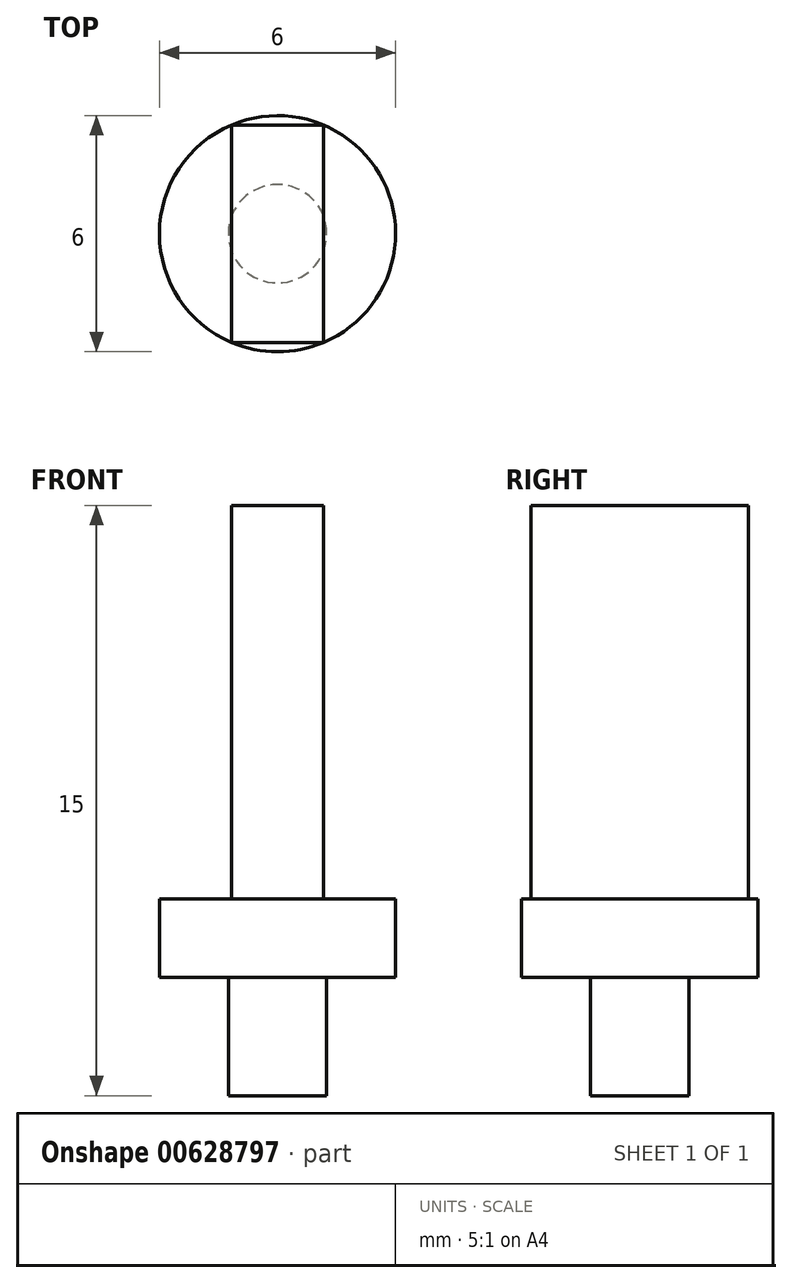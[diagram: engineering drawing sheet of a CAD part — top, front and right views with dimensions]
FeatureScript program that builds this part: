
annotation { "Feature Type Name" : "Feature", "Feature Type Description" : "" }
export const myFeature = defineFeature(function(context is Context, id is Id, definition is map)
    precondition{}
    {
        {
            var Q0;
            Q0=qCreatedBy(makeId("Top.planeOp"),FACE);
            var sketch = newSketch(context, id + "F0", { "sketchPlane" : qUnion([Q0])});
            skCircle(sketch, "E0", {"center": v(0, 0) * mm, "radius": 1.25 * mm});
            skSolve(sketch);
        }
        {
            var Q0;
            Q0 = qSketchRegion(id + "F0", true);
            extrude(context, id + "F1", {"entities" : qUnion([Q0]), "depth" : 3 * mm, "offsetDistance" : 25 * mm});
        }
        {
            var Q0;
            Q0=makeQuery(id+"F1.opExtrude","CAP_FACE",FACE,{"disambiguationData":[OSD([sQuery(id+"F0.wireOp",EDGE,"E0")])],"isStart":false});
            var sketch = newSketch(context, id + "F2", { "sketchPlane" : qUnion([Q0])});
            skCircle(sketch, "E1", {"center": v(0, 0) * mm, "radius": 3 * mm});
            skSolve(sketch);
        }
        {
            var Q0;
            Q0 = qSketchRegion(id + "F2", true);
            extrude(context, id + "F3", {"entities" : qUnion([Q0]), "operationType" : NewBodyOperationType.ADD, "depth" : 2 * mm, "offsetDistance" : 25 * mm});
        }
        {
            var Q0;
            Q0=makeQuery(id+"F3.opExtrude","CAP_FACE",FACE,{"disambiguationData":[OSD([sQuery(id+"F2.wireOp",EDGE,"E1")])],"isStart":false});
            var sketch = newSketch(context, id + "F4", { "sketchPlane" : qUnion([Q0])});
            skLineSegment(sketch, "E2.bottom", {"start": v(-1.17, 2.76) * mm, "end": v(1.16, 2.76) * mm});
            skLineSegment(sketch, "E2.top", {"start": v(-1.17, -2.77) * mm, "end": v(1.16, -2.77) * mm});
            skLineSegment(sketch, "E2.left", {"start": v(-1.17, 2.76) * mm, "end": v(-1.17, -2.77) * mm});
            skLineSegment(sketch, "E2.right", {"start": v(1.16, 2.76) * mm, "end": v(1.16, -2.77) * mm});
            skSolve(sketch);
        }
        {
            var Q0;
            Q0 = qSketchRegion(id + "F4", true);
            extrude(context, id + "F5", {"entities" : qUnion([Q0]), "operationType" : NewBodyOperationType.ADD, "depth" : 10 * mm, "offsetDistance" : 25 * mm});
        }
    });
